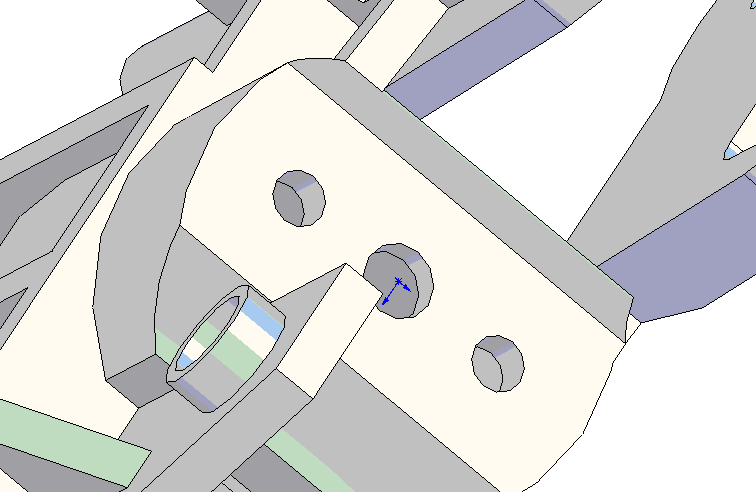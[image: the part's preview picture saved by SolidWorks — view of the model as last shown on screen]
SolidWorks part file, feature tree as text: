
SOLIDWORKS PART (.sldprt)
format: sldprt  version: not decoded by parser v0  size: 866,304 bytes
history: native  units: mm
features: sketch x28, extrude x22, plane x6, cut_extrude x6, fillet x2, material x1, pattern_linear x1 (+10 scaffold rows collapsed)
feature tree (76):
  scaffold x10  (default folders/planes/origin — collapsed)
  material  "Matériau <non spécifié>"
  plane  "Plan de face"
  plane  "Plan de dessus"
  plane  "Plan de droite"
  sketch  "Esquisse1"  dims[c1.D1=8.0mm c1.D2=10.0mm c1.D5=4.0mm c1.D6=5.0mm c1.D7=~4.817417mm c2.D5=1.6mm c2.D7=1.2mm c2.D8=1.2mm c2.D3=3.0mm c2.D4=3.0mm c2.D1=4.0mm c2.D2=4.0mm c3.D3=2.7mm c3.D4=2.7mm]
  extrude  "Extrusion1"  Depth=1mm
  sketch  "Esquisse3"  dims[D3=4.0mm D6=5.0mm D1=3.0mm D2=3.0mm D4=4.0mm D5=4.0mm]
  extrude  "Extrusion2"  Depth=9mm
  sketch  "Esquisse19"  dims[D2=2.4mm D1=3.0mm D3=4.0mm]
  cut_extrude  "Enlèv. mat.-Extru.3"  Depth=10mm
  sketch  "Esquisse4"  dims[D1=1.0mm D2=1.0mm D3=3.3mm D4=3.3mm D5=8.0mm D6=8.0mm D7=0.5mm D8=0.5mm D9=3.0mm]
  extrude  "Extrusion3"  Depth=6mm
  sketch  "Esquisse6"  dims[D1=1.8mm D2=1.8mm D3=0.5mm D4=0.5mm D5=7.6mm D6=7.6mm]
  extrude  "Extrusion5"  Depth=11mm
  sketch  "Esquisse7"  dims[c1.D1=2.0mm c1.D2=5.4mm c1.D3=~0.686077mm c1.D4=~4.713923mm c2.D3=4.1mm c2.D2=1.7mm c2.D4=1.0mm c2.D5=12.0mm c2.D6=0.5mm c3.D3=3.6mm c3.D6=0.5mm c3.D7=3.0mm c3.D8=10.0mm c3.D9=2.0mm c3.D1=0.5mm c3.D10=5.2mm]
  extrude  "Extrusion6"  Depth=1mm
  sketch  "Esquisse8"  dims[c1.D1=6.0mm c1.D2=1.0mm c1.D3=1.0mm c1.D4=14.5mm c1.D5=1.0mm c1.D6=2.0mm c1.D7=1.0mm c1.D8=~3.423293mm c2.D8=135.0deg]
  extrude  "Extrusion7"  Depth=3mm
  sketch  "Esquisse10"  dims[D3=4.0mm D4=4.0mm D1=3.0mm D2=3.0mm]
  cut_extrude  "Enlèv. mat.-Extru.1"  Depth=20mm
  sketch  "Esquisse11"  dims[c1.D1=1.0mm c1.D2=1.0mm c1.D3=0.5mm c1.D4=0.5mm c2.D2=1.0mm c2.D4=0.5mm]
  extrude  "Extrusion8"  Depth=5mm
  sketch  "Esquisse13"  dims[c1.D1=7.0mm c1.D2=7.0mm c1.D3=~2.20195mm c1.D4=17.0mm c1.D5=2.2mm c1.D6=7.8mm c1.D7=9.0mm c2.D4=7.8mm c2.D7=4.23mm c2.D8=~4.23195mm]
  cut_extrude  "Enlèv. mat.-Extru.2"  Depth=20mm
  sketch  "Esquisse12"  dims[c1.D1=3.2mm c1.D2=~1.192253mm c1.D4=1.0mm c1.D5=1.0mm c1.D6=2.5mm c1.D7=1.0mm c1.D8=3.2mm c1.D9=3.2mm c2.D8=1.0mm c2.D10=3.2mm c2.D9=1.0mm c2.D11=3.2mm c2.D6=2.5mm c2.D13=2.5mm c2.D14=2.5mm c2.D18=2.0mm c2.D19=2.0mm c2.D2=8.0mm c2.D3=7.8mm c2.D7=3.2mm c2.D1=3.2mm c3.D10=3.2mm c3.D8=3.2mm c3.D9=3.2mm c3.D12=~5.233154mm c4.D12=30.0deg c4.D13=3.0mm c4.D14=2.0mm c4.D15=8.0mm c4.D16=2.5mm c4.D17=9.0mm c5.D17=30.0deg c5.D19=2.5mm c5.D20=2.0mm c5.D3=7.8mm c5.D21=2.3mm c5.D22=5.0mm c5.D23=1.5mm c5.D24=5.0mm c5.D12=1.5mm c6.D12=30.0deg]
  extrude  "Extrusion9"  Depth=1mm
  sketch  "Esquisse15"  dims[D1=3.2mm D2=3.2mm]
  extrude  "Extrusion11"  Depth=2mm
  sketch  "Esquisse14"  dims[c1.D1=2.6mm c1.D9=2.0mm c1.D2=1.0mm c1.D3=1.0mm c1.D4=2.7mm c1.D5=0.7mm c1.D6=1.45mm c1.D7=0.7mm c1.D8=~0.697055mm c2.D9=1.45mm c2.D10=1.0mm c2.D11=1.0mm c2.D12=1.0mm c2.D13=1.0mm c3.D9=5.0mm]
  extrude  "Extrusion10"  Depth=1mm
  plane  "Plan1"  Offset=4.8mm
  sketch  "Esquisse18"  dims[c1.D1=3.2mm c1.D2=5.0mm c1.D3=5.0mm c1.D4=~4.651166mm c2.D1=5.0mm c2.D2=~6.329424mm]
  extrude  "Extrusion13"  Depth=1mm
  sketch  "Esquisse21"  dims[c1.D1=3.2mm c1.D2=3.2mm c1.D3=3.2mm c2.D2=0.5mm c2.D3=0.5mm]
  extrude  "Extrusion14"  Depth=1mm
  sketch  "Esquisse22"  dims[D1=1.0mm]
  extrude  "Extrusion15"  Depth=5mm
  sketch  "Esquisse23"
  extrude  "Extrusion16"  Depth=7mm
  fillet  "Congé1"  Radius=1mm
  fillet  "Congé2"  Radius=2mm
  sketch  "Esquisse24"  dims[D1=5.0mm D2=3.0mm]
  extrude  "Extrusion17"  Depth=7mm
  sketch  "Esquisse25"  dims[D1=~3.130595mm D2=2.0mm D3=2.0mm D4=~2.535898mm]
  extrude  "Extrusion18"  Depth=2mm
  sketch  "Esquisse26"
  extrude  "Extrusion19"  Depth=1mm
  sketch  "Esquisse27"
  extrude  "Extrusion23"  Depth=1mm
  pattern_linear  "Répétition linéaire2"  Count1=2 Count2=1 Spacing1=3.5mm Spacing2=1mm
  plane  "Plan2"
  sketch  "Esquisse29"  dims[D4=0.7mm D1=2.2mm D2=2.2mm D3=2.2mm]
  cut_extrude  "Enlèv. mat.-Extru.4"  Depth=1mm
  sketch  "Esquisse30"
  extrude  "Extrusion25"  Depth=1mm
  plane  "Plan3"  Offset=7.3mm
  sketch  "Esquisse31"
  extrude  "Extrusion26"  Depth=1mm
  sketch  "Esquisse34"
  extrude  "Extrusion27"  Depth=1mm
  sketch  "Esquisse32"  dims[D1=0.8mm D2=0.8mm]
  cut_extrude  "Enlèv. mat.-Extru.5"  Depth=6mm
  sketch  "Esquisse33"  dims[D1=3.4mm]
  cut_extrude  "Enlèv. mat.-Extru.6"  Depth=0.3mm
  sketch  "Esquisse35"  dims[D1=0.0mm]
  extrude  "Extrusion28"  Depth=1mm
decode coverage: 53 of 59 modeling features carry decoded parameters
note: ~ marks probable driven/reference dimensions
note: suppression state not decoded; provenance and decode notes live in map.json
